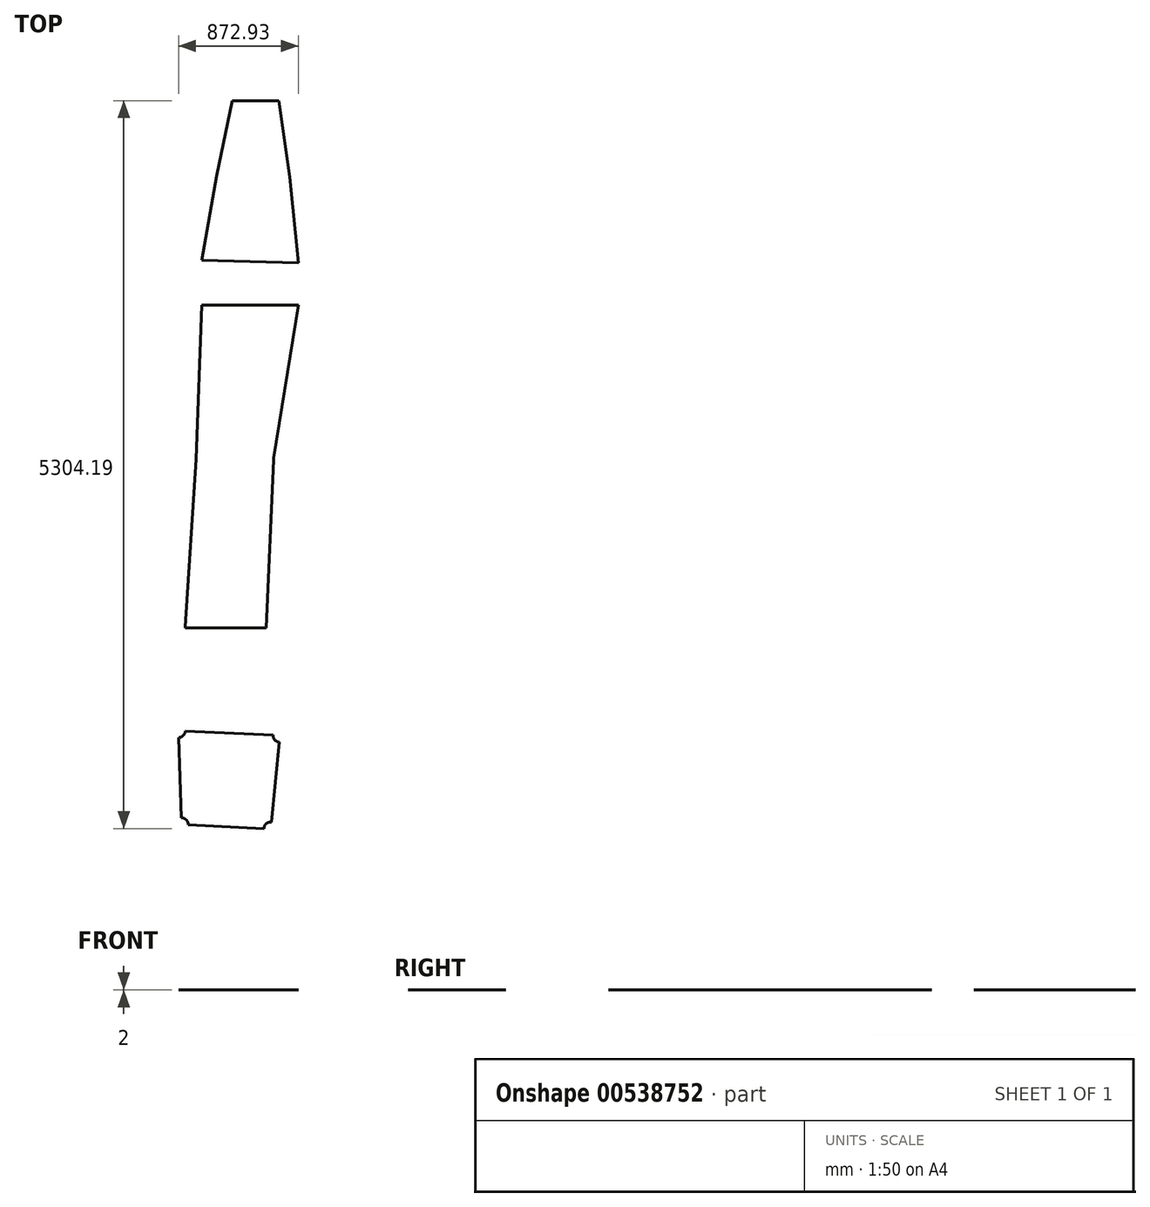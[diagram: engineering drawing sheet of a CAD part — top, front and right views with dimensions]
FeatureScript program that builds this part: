
annotation { "Feature Type Name" : "Feature", "Feature Type Description" : "" }
export const myFeature = defineFeature(function(context is Context, id is Id, definition is map)
    precondition{}
    {
        {
            var Q0;
            Q0=qCreatedBy(makeId("Right.planeOp"),FACE);
            var sketch = newSketch(context, id + "F0", { "sketchPlane" : qUnion([Q0])});
            skLineSegment(sketch, "E0", {"start": v(-2233.25, 0) * mm, "end": v(4416.75, 0) * mm});
            skLineSegment(sketch, "E1", {"start": v(-1678.32, 373.18) * mm, "end": v(4959.24, 461.8) * mm});
            skCircle(sketch, "E2", {"center": v(3439.5, 1256.55) * mm, "radius": 75 * mm});
            skCircle(sketch, "E3", {"center": v(-937.2, 980.17) * mm, "radius": 75 * mm});
            skLineSegment(sketch, "E4", {"start": v(-862.22, 978.06) * mm, "end": v(3364.5, 1256.55) * mm});
            skLineSegment(sketch, "E5", {"start": v(1961.91, 1786.84) * mm, "end": v(3458, 1329.23) * mm, "construction": true});
            skLineSegment(sketch, "E6", {"start": v(2117.1, 1564.3) * mm, "end": v(3166, 1243.47) * mm, "construction": true});
            skLineSegment(sketch, "E7", {"start": v(1942.73, 1556.22) * mm, "end": v(1968.54, 1164.57) * mm});
            skCircle(sketch, "E8", {"center": v(3439.5, 1256.55) * mm, "radius": 100 * mm});
            skArc(sketch, "E9", {"start": v(3519.98, 1315.92) * mm, "mid": v(2777.45, 1786.86) * mm, "end": v(1915.96, 1962.82) * mm});
            skLineSegment(sketch, "E10", {"start": v(1809.91, 1154.12) * mm, "end": v(1823.06, 954.56) * mm});
            skLineSegment(sketch, "E11", {"start": v(1823.06, 954.56) * mm, "end": v(3229.84, 1047.24) * mm});
            skArc(sketch, "E12", {"start": v(3229.84, 1047.24) * mm, "mid": v(3392.66, 1093.16) * mm, "end": v(3522.81, 1201.23) * mm});
            skLineSegment(sketch, "E13", {"start": v(1968.54, 1164.57) * mm, "end": v(1981.68, 965) * mm});
            skLineSegment(sketch, "E14", {"start": v(2854.82, 1222.97) * mm, "end": v(2818.8, 1769.75) * mm, "construction": true});
            skLineSegment(sketch, "E15", {"start": v(1942.73, 1556.22) * mm, "end": v(2017.58, 1561.04) * mm});
            skLineSegment(sketch, "E16", {"start": v(2017.58, 1561.04) * mm, "end": v(2043.22, 1171.89) * mm});
            skLineSegment(sketch, "E17", {"start": v(2043.22, 1171.89) * mm, "end": v(1893.72, 1159.64) * mm});
            skLineSegment(sketch, "E18", {"start": v(1893.72, 1159.64) * mm, "end": v(1868.08, 1548.8) * mm});
            skLineSegment(sketch, "E19", {"start": v(1868.08, 1548.8) * mm, "end": v(1942.73, 1556.22) * mm});
            skLineSegment(sketch, "E20", {"start": v(2043.22, 1171.89) * mm, "end": v(1991.28, 1960.18) * mm});
            skLineSegment(sketch, "E21", {"start": v(3229.84, 1047.24) * mm, "end": v(3195.46, 1569) * mm, "construction": true});
            skText(sketch, "E22", { "text": "ali se bo videlo čez kabino!?\n", "fontName": "Arimo-Regular.ttf"});
            skLineSegment(sketch, "E23", {"start": v(-1540.21, 973.83) * mm, "end": v(5413.74, 1432) * mm});
            skLineSegment(sketch, "E24", {"start": v(-914, 2441.94) * mm, "end": v(1763.64, 2441.94) * mm});
            skLineSegment(sketch, "E25", {"start": v(4233.64, 1983.74) * mm, "end": v(2114.45, 1983.74) * mm});
            skLineSegment(sketch, "E26", {"start": v(-1229, 2363.19) * mm, "end": v(1785.12, 2019.54) * mm});
            const initialGuessF0  = {"E22": [-0.50932, 3.05584, 1, 0, 0.22235]};
            skSetInitialGuess(sketch, initialGuessF0);
            skSolve(sketch);
        }
        {
            var Q0;
            Q0=qCreatedBy(makeId("Top.planeOp"),FACE);
            var sketch = newSketch(context, id + "F1", { "sketchPlane" : qUnion([Q0])});
            skLineSegment(sketch, "E27", {"start": v(0, 5428.34) * mm, "end": v(1650, 5428.34) * mm});
            skLineSegment(sketch, "E28.MirrorCS", {"start": v(0, 5428.34) * mm, "end": v(-1650, 5428.34) * mm});
            skLineSegment(sketch, "E29", {"start": v(0, 1787.86) * mm, "end": v(2150, 1787.86) * mm});
            skLineSegment(sketch, "E30.MirrorCS", {"start": v(0, 1787.86) * mm, "end": v(-2150, 1787.86) * mm});
            skLineSegment(sketch, "E31", {"start": v(-1103.65, 2449.14) * mm, "end": v(900.2, 2379.56) * mm});
            skLineSegment(sketch, "E32", {"start": v(-2046.24, 3487.1) * mm, "end": v(1952.86, 3402.44) * mm});
            skLineSegment(sketch, "E33.bottom", {"start": v(-1171.41, 3343.27) * mm, "end": v(1096.05, 3343.27) * mm});
            skLineSegment(sketch, "E33.top", {"start": v(-1171.41, 3049.83) * mm, "end": v(1096.05, 3049.83) * mm});
            skLineSegment(sketch, "E33.left", {"start": v(-1171.41, 3343.27) * mm, "end": v(-1171.41, 3049.83) * mm});
            skLineSegment(sketch, "E33.right", {"start": v(1096.05, 3343.27) * mm, "end": v(1096.05, 3049.83) * mm});
            skLineSegment(sketch, "E34.bottom", {"start": v(-1176.75, 2991.14) * mm, "end": v(1032.03, 2991.14) * mm});
            skLineSegment(sketch, "E34.top", {"start": v(-1176.75, 2238.88) * mm, "end": v(1032.03, 2238.88) * mm});
            skLineSegment(sketch, "E34.left", {"start": v(-1176.75, 2991.14) * mm, "end": v(-1176.75, 2238.88) * mm});
            skLineSegment(sketch, "E34.right", {"start": v(1032.03, 2991.14) * mm, "end": v(1032.03, 2238.88) * mm});
            skLineSegment(sketch, "E35.top", {"start": v(-1176.75, 2025.47) * mm, "end": v(1032.03, 2025.47) * mm});
            skLineSegment(sketch, "E35.left", {"start": v(-1176.75, 2238.88) * mm, "end": v(-1176.75, 2025.47) * mm});
            skLineSegment(sketch, "E35.right", {"start": v(1032.03, 2238.88) * mm, "end": v(1032.03, 2025.47) * mm});
            skLineSegment(sketch, "E36", {"start": v(-1543.42, 2127.47) * mm, "end": v(-1601.38, 928.56) * mm});
            skLineSegment(sketch, "E37", {"start": v(-2123.04, 928.56) * mm, "end": v(-1601.38, 903.34) * mm});
            skLineSegment(sketch, "E38", {"start": v(-1792.43, 4697.27) * mm, "end": v(-1441.6, 4697.27) * mm});
            skLineSegment(sketch, "E39", {"start": v(-1441.6, 4697.27) * mm, "end": v(-1420.25, 3959) * mm});
            skLineSegment(sketch, "E40", {"start": v(-2061.73, 2453.79) * mm, "end": v(-1818.66, 2453.79) * mm});
            skLineSegment(sketch, "E41", {"start": v(-1818.66, 2453.79) * mm, "end": v(-1786, 3161.23) * mm});
            skSolve(sketch);
        }
        {
            var Q0;
            Q0=makeQuery(id+"F1.imprint","IMPRINT",FACE,{"disambiguationData":[TD([[makeQuery(id+"F1.imprint","IMPRINT",EDGE,{"derivedFrom":sQuery(id+"F1.wireOp",EDGE,"E34.bottom")}),-1.0]])]});
            var sketch = newSketch(context, id + "F2", { "sketchPlane" : qUnion([Q0])});
            skCircle(sketch, "E42", {"center": v(-1613.53, 4825.48) * mm, "radius": 50 * mm});
            skCircle(sketch, "E43", {"center": v(-1820.8, 4803.78) * mm, "radius": 50 * mm});
            skCircle(sketch, "E44", {"center": v(-2043.81, 3574.26) * mm, "radius": 50 * mm});
            skCircle(sketch, "E45", {"center": v(-1413.54, 4810.04) * mm, "radius": 50 * mm});
            skCircle(sketch, "E46", {"center": v(-1946.65, 4230.42) * mm, "radius": 50 * mm});
            skCircle(sketch, "E47", {"center": v(-1317.46, 4219.88) * mm, "radius": 50 * mm});
            skCircle(sketch, "E48", {"center": v(-1264.54, 3556.32) * mm, "radius": 50 * mm});
            skLineSegment(sketch, "E49", {"start": v(-1783.99, 4769.95) * mm, "end": v(-1443.42, 4769.95) * mm});
            skLineSegment(sketch, "E50", {"start": v(-1443.42, 4769.95) * mm, "end": v(-1367, 4213.08) * mm});
            skLineSegment(sketch, "E51", {"start": v(-1367, 4213.08) * mm, "end": v(-1302.4, 3588.99) * mm});
            skLineSegment(sketch, "E52", {"start": v(-1302.4, 3588.99) * mm, "end": v(-2007.32, 3608.44) * mm});
            skLineSegment(sketch, "E53", {"start": v(-2007.32, 3608.44) * mm, "end": v(-1897.43, 4221.6) * mm});
            skLineSegment(sketch, "E54", {"start": v(-1897.43, 4221.6) * mm, "end": v(-1783.99, 4769.95) * mm});
            skCircle(sketch, "E55", {"center": v(-2062.2, 3326.03) * mm, "radius": 50 * mm});
            skCircle(sketch, "E56", {"center": v(-1262.26, 3311.02) * mm, "radius": 50 * mm});
            skCircle(sketch, "E57", {"center": v(-2176.75, 936.4) * mm, "radius": 50 * mm});
            skCircle(sketch, "E58", {"center": v(-1485.54, 925.67) * mm, "radius": 50 * mm});
            skCircle(sketch, "E59", {"center": v(-1433.4, 2157.85) * mm, "radius": 50 * mm});
            skCircle(sketch, "E60", {"center": v(-2098.75, 2158.97) * mm, "radius": 50 * mm});
            skLineSegment(sketch, "E61", {"start": v(-2007.32, 3281.56) * mm, "end": v(-1302.67, 3281.56) * mm});
            skLineSegment(sketch, "E62", {"start": v(-1302.67, 3281.56) * mm, "end": v(-1482.77, 2165.82) * mm});
            skLineSegment(sketch, "E63", {"start": v(-1482.77, 2165.82) * mm, "end": v(-1535.5, 927.8) * mm});
            skLineSegment(sketch, "E64", {"start": v(-1535.5, 927.8) * mm, "end": v(-2127.5, 927.8) * mm});
            skLineSegment(sketch, "E65", {"start": v(-2127.5, 927.8) * mm, "end": v(-2048.85, 2155.78) * mm});
            skLineSegment(sketch, "E66", {"start": v(-2048.85, 2155.78) * mm, "end": v(-2007.32, 3281.56) * mm});
            skCircle(sketch, "E67", {"center": v(-2176.9, 178.66) * mm, "radius": 50 * mm});
            skCircle(sketch, "E68", {"center": v(-1437.48, 145.43) * mm, "radius": 50 * mm});
            skCircle(sketch, "E69", {"center": v(-2155.33, -505.8) * mm, "radius": 50 * mm});
            skCircle(sketch, "E70", {"center": v(-1504.18, -536.6) * mm, "radius": 50 * mm});
            skLineSegment(sketch, "E71", {"start": v(-2176.9, 178.66) * mm, "end": v(-2155.33, -505.8) * mm});
            skLineSegment(sketch, "E72", {"start": v(-1504.18, -536.6) * mm, "end": v(-2155.33, -505.8) * mm});
            skLineSegment(sketch, "E73", {"start": v(-1437.48, 145.43) * mm, "end": v(-1504.18, -536.6) * mm});
            skLineSegment(sketch, "E74", {"start": v(-1437.48, 145.43) * mm, "end": v(-2176.9, 178.66) * mm});
            skSolve(sketch);
        }
        {
            var Q0;
            Q0=makeQuery(id+"F2.imprint","IMPRINT",FACE,{"disambiguationData":[TD([[makeQuery(id+"F2.imprint","IMPRINT",EDGE,{"derivedFrom":sQuery(id+"F2.wireOp",EDGE,"E49")}),-1.0]])]});
            extrude(context, id + "F3", {"entities" : qUnion([Q0]), "depth" : 2 * mm, "offsetDistance" : 25 * mm});
        }
        {
            var Q0;
            {var subQ0=sQuery(id+"F2.wireOp",EDGE,"E61");Q0=makeQuery(id+"F2.imprint","IMPRINT",FACE,{"disambiguationData":[TD([[makeQuery(id+"F2.imprint","IMPRINT",EDGE,{"derivedFrom":subQ0}),-1.0]])]});}
            extrude(context, id + "F4", {"entities" : qUnion([Q0]), "depth" : 2 * mm, "offsetDistance" : 25 * mm});
        }
        {
            var Q0;
            {var subQ9=sQuery(id+"F2.wireOp",EDGE,"E71");var subQ13=sQuery(id+"F2.wireOp",EDGE,"E67");var subQ14=makeQuery(id+"F2.imprint","INTERSECT",VERTEX,{"derivedFrom":[subQ13,subQ9]});Q0=makeQuery(id+"F2.imprint","IMPRINT",FACE,{"disambiguationData":[TD([[makeQuery(id+"F2.imprint","IMPRINT",EDGE,{"disambiguationData":[TD([[subQ14,-1.0]])],"derivedFrom":subQ13}),-1.0]])]});}
            extrude(context, id + "F5", {"entities" : qUnion([Q0]), "depth" : 2 * mm, "offsetDistance" : 25 * mm});
        }
    });
